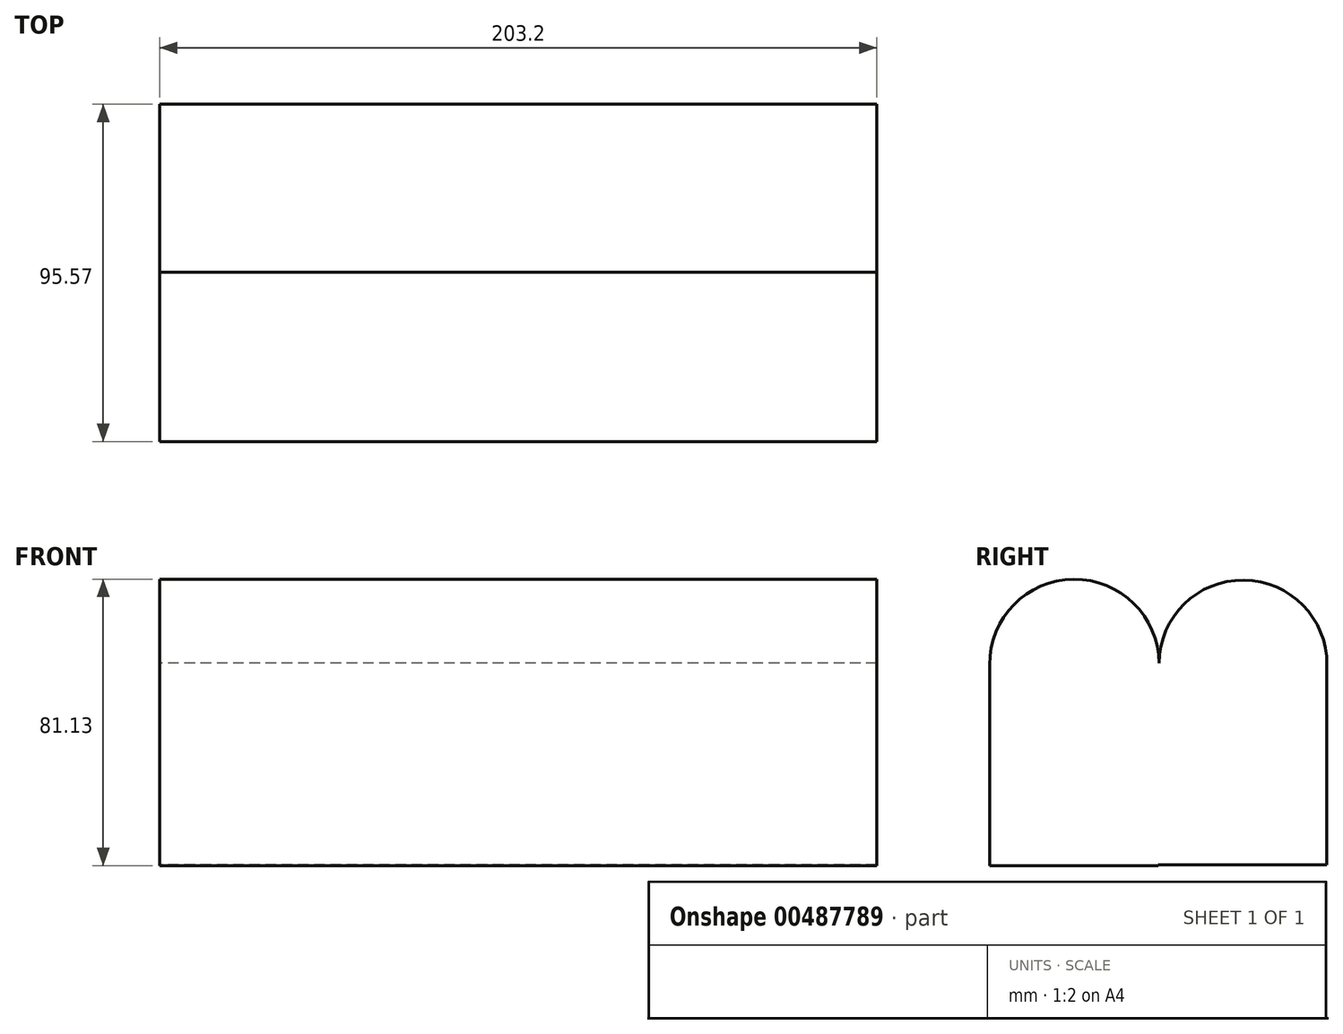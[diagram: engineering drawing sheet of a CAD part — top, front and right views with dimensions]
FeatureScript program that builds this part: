
annotation { "Feature Type Name" : "Feature", "Feature Type Description" : "" }
export const myFeature = defineFeature(function(context is Context, id is Id, definition is map)
    precondition{}
    {
        {
            var Q0;
            Q0=qCreatedBy(makeId("Right.planeOp"),FACE);
            var sketch = newSketch(context, id + "F0", { "sketchPlane" : qUnion([Q0])});
            skLineSegment(sketch, "E0.bottom", {"start": v(-47.78, 0) * mm, "end": v(0, 0) * mm});
            skLineSegment(sketch, "E0.top", {"start": v(-47.78, -56.9) * mm, "end": v(0, -56.9) * mm});
            skLineSegment(sketch, "E0.left", {"start": v(-47.78, 0) * mm, "end": v(-47.78, -56.9) * mm});
            skLineSegment(sketch, "E0.right", {"start": v(0, 0) * mm, "end": v(0, -56.9) * mm});
            skLineSegment(sketch, "E1.bottom", {"start": v(0, 0) * mm, "end": v(47.79, 0) * mm});
            skLineSegment(sketch, "E1.top", {"start": v(0, -56.68) * mm, "end": v(47.79, -56.68) * mm});
            skLineSegment(sketch, "E1.left", {"start": v(0, 0) * mm, "end": v(0, -56.68) * mm});
            skLineSegment(sketch, "E1.right", {"start": v(47.79, 0) * mm, "end": v(47.79, -56.68) * mm});
            skArc(sketch, "E2", {"start": v(0.22, 0.44) * mm, "mid": v(-24, 24.22) * mm, "end": v(-47.78, 0) * mm});
            skArc(sketch, "E3", {"start": v(47.79, 0) * mm, "mid": v(24.23, 24) * mm, "end": v(0.22, 0.44) * mm});
            skSolve(sketch);
        }
        {
            var Q0;
            Q0=makeQuery(id+"F0.imprint","IMPRINT",FACE,{"disambiguationData":[TD([[makeQuery(id+"F0.imprint","IMPRINT",EDGE,{"derivedFrom":sQuery(id+"F0.wireOp",EDGE,"E0.bottom")}),-1.0]])]});
            var Q1;
            Q1=makeQuery(id+"F0.imprint","IMPRINT",FACE,{"disambiguationData":[TD([[makeQuery(id+"F0.imprint","IMPRINT",EDGE,{"derivedFrom":sQuery(id+"F0.wireOp",EDGE,"E1.bottom")}),-1.0]])]});
            var Q2;
            Q2=makeQuery(id+"F0.imprint","IMPRINT",FACE,{"disambiguationData":[TD([[makeQuery(id+"F0.imprint","IMPRINT",EDGE,{"derivedFrom":sQuery(id+"F0.wireOp",EDGE,"E0.bottom")}),1.0]])]});
            extrude(context, id + "F1", {"entities" : qUnion([Q0, Q1, Q2]), "depth" : 203.2 * mm});
        }
    });
